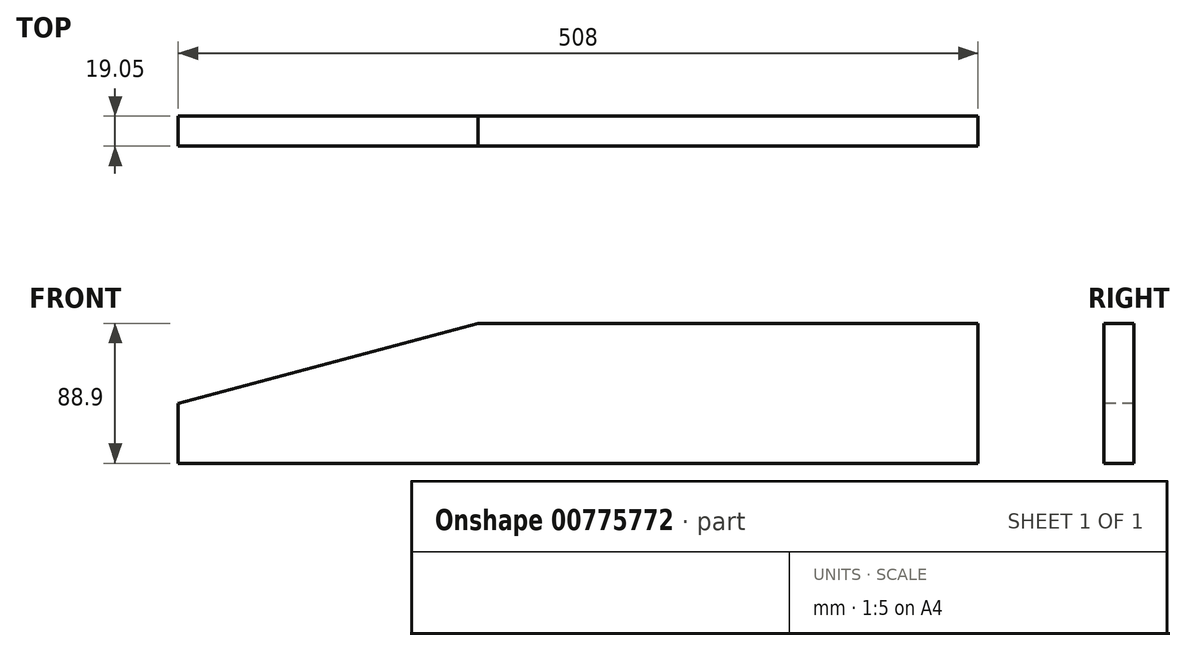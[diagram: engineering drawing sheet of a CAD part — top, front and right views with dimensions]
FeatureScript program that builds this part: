
annotation { "Feature Type Name" : "Feature", "Feature Type Description" : "" }
export const myFeature = defineFeature(function(context is Context, id is Id, definition is map)
    precondition{}
    {
        {
            var Q0;
            Q0=qCreatedBy(makeId("Front.planeOp"),FACE);
            var sketch = newSketch(context, id + "F0", { "sketchPlane" : qUnion([Q0])});
            skLineSegment(sketch, "E0.bottom", {"start": v(0, 0) * mm, "end": v(508, 0) * mm});
            skLineSegment(sketch, "E0.top", {"start": v(0, 88.9) * mm, "end": v(508, 88.9) * mm});
            skLineSegment(sketch, "E0.left", {"start": v(0, 0) * mm, "end": v(0, 88.9) * mm});
            skLineSegment(sketch, "E0.right", {"start": v(508, 0) * mm, "end": v(508, 88.9) * mm});
            skLineSegment(sketch, "E1", {"start": v(0, 44.45) * mm, "end": v(190.5, 88.9) * mm});
            skSolve(sketch);
        }
        {
            var Q0;
            Q0 = qSketchRegion(id + "F0", true);
            extrude(context, id + "F1", {"entities" : qUnion([Q0]), "depth" : 19.05 * mm, "offsetDistance" : 25.4 * mm});
        }
        {
            var Q0;
            Q0=makeQuery(id+"F1.opExtrude","CAP_FACE",FACE,{"disambiguationData":[OSD([sQuery(id+"F0.wireOp",EDGE,"E0.bottom"),sQuery(id+"F0.wireOp",EDGE,"E0.top"),sQuery(id+"F0.wireOp",EDGE,"E0.left"),sQuery(id+"F0.wireOp",EDGE,"E0.right")])],"isStart":false});
            var sketch = newSketch(context, id + "F2", { "sketchPlane" : qUnion([Q0])});
            skLineSegment(sketch, "E2", {"start": v(190.5, 88.9) * mm, "end": v(0, 88.9) * mm});
            skLineSegment(sketch, "E3", {"start": v(0, 88.9) * mm, "end": v(0, 38.1) * mm});
            skLineSegment(sketch, "E4", {"start": v(0, 38.1) * mm, "end": v(190.5, 88.9) * mm});
            skSolve(sketch);
        }
        {
            var Q0;
            Q0=makeQuery(id+"F2.imprint","IMPRINT",FACE,{"disambiguationData":[TD([[makeQuery(id+"F2.imprint","IMPRINT",EDGE,{"derivedFrom":sQuery(id+"F2.wireOp",EDGE,"E2")}),-1.0]])]});
            extrude(context, id + "F3", {"entities" : qUnion([Q0]), "operationType" : NewBodyOperationType.REMOVE, "oppositeDirection" : true, "depth" : 25.4 * mm, "offsetDistance" : 25.4 * mm});
        }
    });
